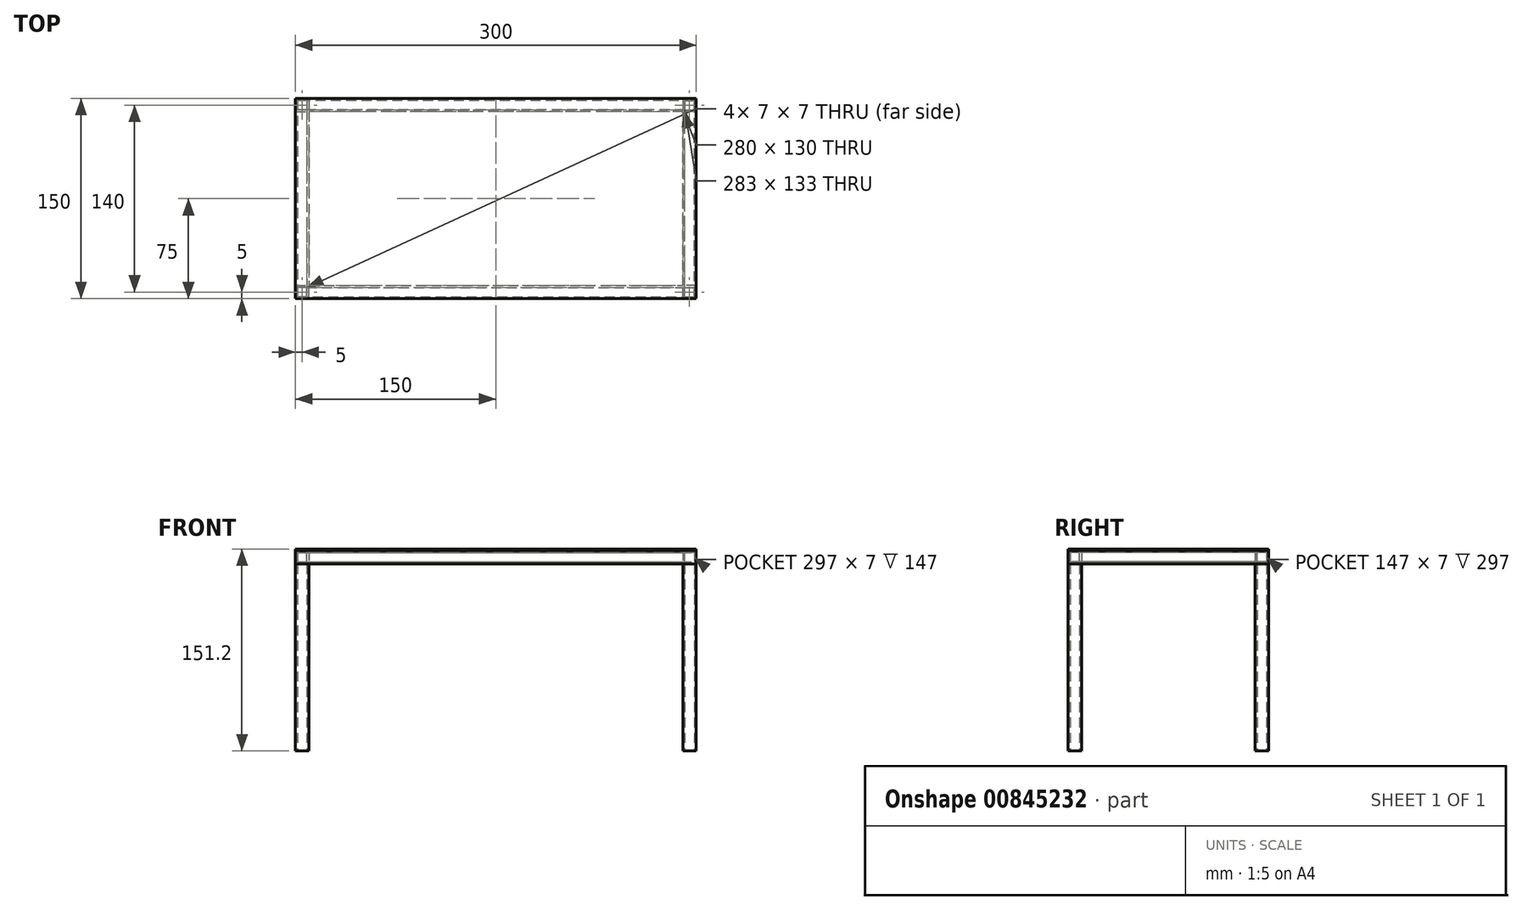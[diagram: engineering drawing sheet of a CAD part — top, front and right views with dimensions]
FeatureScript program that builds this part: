
annotation { "Feature Type Name" : "Feature", "Feature Type Description" : "" }
export const myFeature = defineFeature(function(context is Context, id is Id, definition is map)
    precondition{}
    {
        {
            var Q0;
            Q0=qCreatedBy(makeId("Top.planeOp"),FACE);
            var sketch = newSketch(context, id + "F0", { "sketchPlane" : qUnion([Q0])});
            skLineSegment(sketch, "E0.bottom", {"start": v(-150, 75) * mm, "end": v(-140, 75) * mm});
            skLineSegment(sketch, "E0.top", {"start": v(-150, 65) * mm, "end": v(-140, 65) * mm});
            skLineSegment(sketch, "E0.left", {"start": v(-150, 75) * mm, "end": v(-150, 65) * mm});
            skLineSegment(sketch, "E0.right", {"start": v(-140, 75) * mm, "end": v(-140, 65) * mm});
            skLineSegment(sketch, "E1.bottom", {"start": v(-141.5, 73.5) * mm, "end": v(-148.5, 73.5) * mm});
            skLineSegment(sketch, "E1.top", {"start": v(-141.5, 66.5) * mm, "end": v(-148.5, 66.5) * mm});
            skLineSegment(sketch, "E1.left", {"start": v(-141.5, 73.5) * mm, "end": v(-141.5, 66.5) * mm});
            skLineSegment(sketch, "E1.right", {"start": v(-148.5, 73.5) * mm, "end": v(-148.5, 66.5) * mm});
            skPoint(sketch, "E1.middle", {"position": v(-145, 70) * mm});
            skPoint(sketch, "E1.middle.positionSnap0", {"position": v(-145, 75) * mm});
            skPoint(sketch, "E1.middle.positionSnap1", {"position": v(-150, 70) * mm});
            skPoint(sketch, "E1.centerSnap0", {"position": v(-145, 75) * mm});
            skPoint(sketch, "E1.centerSnap1", {"position": v(-150, 70) * mm});
            skLineSegment(sketch, "E2.MirrorCS", {"start": v(150, 75) * mm, "end": v(140, 75) * mm});
            skLineSegment(sketch, "E3.MirrorCS", {"start": v(148.5, 73.5) * mm, "end": v(148.5, 66.5) * mm});
            skLineSegment(sketch, "E4.MirrorCS", {"start": v(150, 75) * mm, "end": v(150, 65) * mm});
            skLineSegment(sketch, "E5.MirrorCS", {"start": v(141.5, 73.5) * mm, "end": v(148.5, 73.5) * mm});
            skPoint(sketch, "E6.MirrorP", {"position": v(145, 75) * mm});
            skPoint(sketch, "E7.MirrorP", {"position": v(150, 70) * mm});
            skLineSegment(sketch, "E8.MirrorCS", {"start": v(141.5, 73.5) * mm, "end": v(141.5, 66.5) * mm});
            skLineSegment(sketch, "E9.MirrorCS", {"start": v(150, 65) * mm, "end": v(140, 65) * mm});
            skPoint(sketch, "E10.MirrorP", {"position": v(145, 70) * mm});
            skLineSegment(sketch, "E11.MirrorCS", {"start": v(140, 75) * mm, "end": v(140, 65) * mm});
            skLineSegment(sketch, "E12.MirrorCS", {"start": v(141.5, 66.5) * mm, "end": v(148.5, 66.5) * mm});
            skLineSegment(sketch, "E13.MirrorCS", {"start": v(141.5, -73.5) * mm, "end": v(141.5, -66.5) * mm});
            skLineSegment(sketch, "E14.MirrorCS", {"start": v(141.5, -73.5) * mm, "end": v(148.5, -73.5) * mm});
            skLineSegment(sketch, "E15.MirrorCS", {"start": v(140, -75) * mm, "end": v(140, -65) * mm});
            skLineSegment(sketch, "E16.MirrorCS", {"start": v(-141.5, -66.5) * mm, "end": v(-148.5, -66.5) * mm});
            skLineSegment(sketch, "E17.MirrorCS", {"start": v(-150, -75) * mm, "end": v(-140, -75) * mm});
            skLineSegment(sketch, "E18.MirrorCS", {"start": v(-150, -65) * mm, "end": v(-140, -65) * mm});
            skLineSegment(sketch, "E19.MirrorCS", {"start": v(-150, -75) * mm, "end": v(-150, -65) * mm});
            skLineSegment(sketch, "E20.MirrorCS", {"start": v(-148.5, -73.5) * mm, "end": v(-148.5, -66.5) * mm});
            skLineSegment(sketch, "E21.MirrorCS", {"start": v(-141.5, -73.5) * mm, "end": v(-141.5, -66.5) * mm});
            skLineSegment(sketch, "E22.MirrorCS", {"start": v(-141.5, -73.5) * mm, "end": v(-148.5, -73.5) * mm});
            skLineSegment(sketch, "E23.MirrorCS", {"start": v(150, -75) * mm, "end": v(140, -75) * mm});
            skLineSegment(sketch, "E24.MirrorCS", {"start": v(150, -75) * mm, "end": v(150, -65) * mm});
            skLineSegment(sketch, "E25.MirrorCS", {"start": v(148.5, -73.5) * mm, "end": v(148.5, -66.5) * mm});
            skLineSegment(sketch, "E26.MirrorCS", {"start": v(-140, -75) * mm, "end": v(-140, -65) * mm});
            skPoint(sketch, "E27.MirrorP", {"position": v(145, -75) * mm});
            skLineSegment(sketch, "E28.MirrorCS", {"start": v(150, -65) * mm, "end": v(140, -65) * mm});
            skLineSegment(sketch, "E29.MirrorCS", {"start": v(141.5, -66.5) * mm, "end": v(148.5, -66.5) * mm});
            skPoint(sketch, "E30.MirrorP", {"position": v(150, -70) * mm});
            skPoint(sketch, "E31.MirrorP", {"position": v(-145, -75) * mm});
            skPoint(sketch, "E32.MirrorP", {"position": v(-150, -70) * mm});
            skPoint(sketch, "E33.MirrorP", {"position": v(-145, -70) * mm});
            skPoint(sketch, "E34.MirrorP", {"position": v(145, -70) * mm});
            skSolve(sketch);
        }
        {
            var Q0;
            Q0 = qSketchRegion(id + "F0", true);
            extrude(context, id + "F1", {"entities" : qUnion([Q0]), "depth" : 140 * mm, "offsetDistance" : 25 * mm});
        }
        {
            var Q0;
            Q0=makeQuery(id+"F1.opExtrude","CAP_FACE",FACE,{"disambiguationData":[OSD([sQuery(id+"F0.wireOp",EDGE,"E16.MirrorCS"),sQuery(id+"F0.wireOp",EDGE,"E17.MirrorCS"),sQuery(id+"F0.wireOp",EDGE,"E18.MirrorCS"),sQuery(id+"F0.wireOp",EDGE,"E19.MirrorCS"),sQuery(id+"F0.wireOp",EDGE,"E20.MirrorCS"),sQuery(id+"F0.wireOp",EDGE,"E21.MirrorCS"),sQuery(id+"F0.wireOp",EDGE,"E22.MirrorCS"),sQuery(id+"F0.wireOp",EDGE,"E26.MirrorCS")])],"isStart":false});
            var sketch = newSketch(context, id + "F2", { "sketchPlane" : qUnion([Q0])});
            skLineSegment(sketch, "E35.bottom", {"start": v(-150, 75) * mm, "end": v(150, 75) * mm});
            skLineSegment(sketch, "E35.top", {"start": v(-150, -75) * mm, "end": v(150, -75) * mm});
            skLineSegment(sketch, "E35.left", {"start": v(-150, 75) * mm, "end": v(-150, -75) * mm});
            skLineSegment(sketch, "E35.right", {"start": v(150, 75) * mm, "end": v(150, -75) * mm});
            skSolve(sketch);
        }
        {
            var Q0;
            Q0=qCreatedBy(makeId("Right.planeOp"),FACE);
            var sketch = newSketch(context, id + "F3", { "sketchPlane" : qUnion([Q0])});
            skLineSegment(sketch, "E36.bottom", {"start": v(-75, 140) * mm, "end": v(-65, 140) * mm});
            skLineSegment(sketch, "E36.top", {"start": v(-75, 150) * mm, "end": v(-65, 150) * mm});
            skLineSegment(sketch, "E36.left", {"start": v(-75, 140) * mm, "end": v(-75, 150) * mm});
            skLineSegment(sketch, "E36.right", {"start": v(-65, 140) * mm, "end": v(-65, 150) * mm});
            skLineSegment(sketch, "E37.bottom", {"start": v(-66.5, 148.5) * mm, "end": v(-73.5, 148.5) * mm});
            skLineSegment(sketch, "E37.top", {"start": v(-66.5, 141.5) * mm, "end": v(-73.5, 141.5) * mm});
            skLineSegment(sketch, "E37.left", {"start": v(-66.5, 148.5) * mm, "end": v(-66.5, 141.5) * mm});
            skLineSegment(sketch, "E37.right", {"start": v(-73.5, 148.5) * mm, "end": v(-73.5, 141.5) * mm});
            skPoint(sketch, "E37.middle", {"position": v(-70, 145) * mm});
            skPoint(sketch, "E37.middle.positionSnap0", {"position": v(-70, 150) * mm});
            skPoint(sketch, "E37.middle.positionSnap1", {"position": v(-75, 145) * mm});
            skPoint(sketch, "E37.centerSnap0", {"position": v(-70, 150) * mm});
            skPoint(sketch, "E37.centerSnap1", {"position": v(-75, 145) * mm});
            skSolve(sketch);
        }
        {
            var Q0;
            Q0=makeQuery(id+"F3.imprint","IMPRINT",FACE,{"disambiguationData":[TD([[makeQuery(id+"F3.imprint","IMPRINT",EDGE,{"derivedFrom":sQuery(id+"F3.wireOp",EDGE,"E36.bottom")}),1.0]])]});
            var Q1;
            Q1=sQuery(id+"F2.wireOp",EDGE,"E35.top");
            var Q2;
            Q2=sQuery(id+"F2.wireOp",EDGE,"E35.right");
            var Q3;
            Q3=sQuery(id+"F2.wireOp",EDGE,"E35.bottom");
            var Q4;
            Q4=sQuery(id+"F2.wireOp",EDGE,"E35.left");
            sweep(context, id + "F4", {"profiles" : qUnion([Q0]), "path" : qUnion([Q1, Q2, Q3, Q4])});
        }
        {
            var Q0;
            Q0=makeQuery(id+"F4.opSweep","SWEPT_FACE",FACE,{"disambiguationData":[OSD([sQuery(id+"F2.wireOp",EDGE,"E35.left"),sQuery(id+"F3.wireOp",EDGE,"E36.top")])]});
            var sketch = newSketch(context, id + "F5", { "sketchPlane" : qUnion([Q0])});
            skLineSegment(sketch, "E38.0", {"start": v(150, 75) * mm, "end": v(-150, 75) * mm});
            skLineSegment(sketch, "E38.1", {"start": v(150, -75) * mm, "end": v(150, 75) * mm});
            skLineSegment(sketch, "E38.2", {"start": v(-150, -75) * mm, "end": v(150, -75) * mm});
            skLineSegment(sketch, "E38.3", {"start": v(-150, 75) * mm, "end": v(-150, -75) * mm});
            skSolve(sketch);
        }
        {
            var Q0;
            Q0 = qSketchRegion(id + "F5", true);
            extrude(context, id + "F6", {"entities" : qUnion([Q0]), "depth" : 1.2 * mm, "offsetDistance" : 25 * mm});
        }
    });
